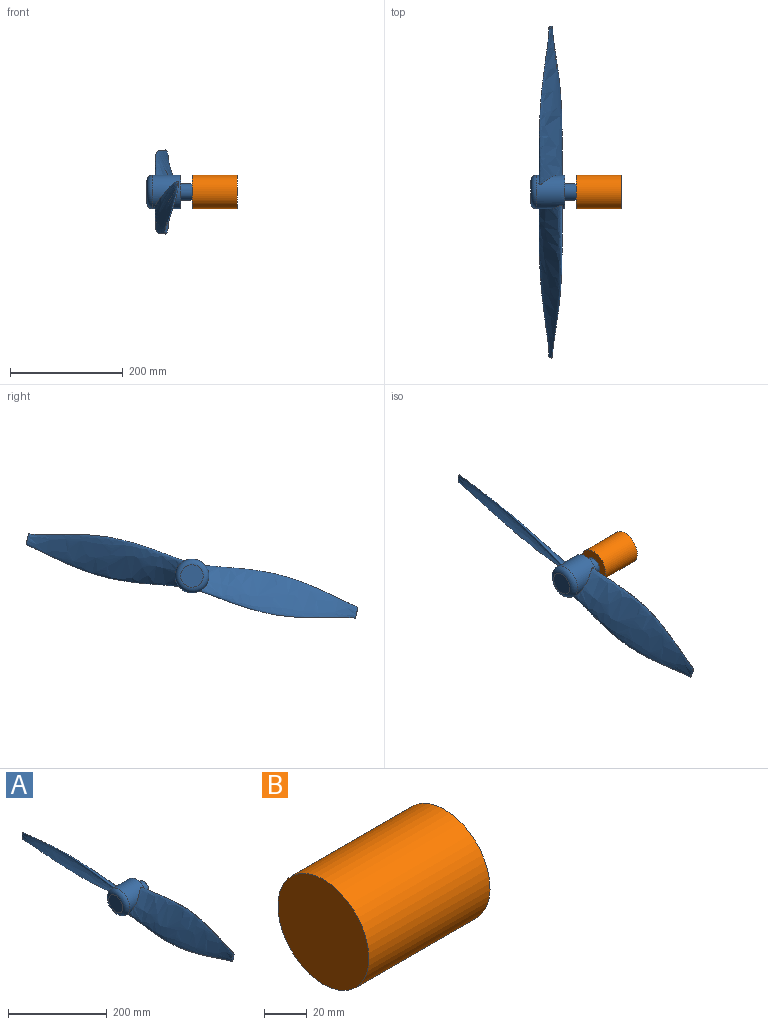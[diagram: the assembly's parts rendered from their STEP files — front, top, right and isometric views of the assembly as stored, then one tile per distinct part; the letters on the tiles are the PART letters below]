
ASSEMBLY  parts=2 mates=1
PART A: 15 faces, bbox 80x600x95 mm
  f0: plane 30x30mm, normal (1,0,0), area 624.5mm2, adj f1,f6,f7,f8,f9
  f1: cylinder r=15mm len=30mm, axis (-1,0,0), area 1885mm2, adj f0,f2
  f2: plane 60x60mm, normal (1,0,0), area 2120.6mm2, adj f1,f3
  f3: cylinder r=30mm len=60mm, axis (-1,0,0), area 8074.1mm2, adj f2,f5,f12,f13
  f4: plane 40x40mm, normal (-1,0,0), area 1256.6mm2, adj f5
  f5: torus R=20mm, axis (1,0,0), area 2602.2mm2, adj f3,f4
  f6: plane 20x2mm, normal (0,-1,0), area 40mm2, adj f0,f7,f9,f10
  f7: cylinder r=5mm len=20mm, axis (1,0,0), area 588mm2, adj f0,f6,f8,f10
  f8: plane 20x2mm, normal (0,1,0), area 40mm2, adj f0,f7,f9,f10
  f9: plane 20x2mm, normal (0,0,1), area 40mm2, adj f0,f6,f8,f10
  f10: plane 11.9x10mm, normal (1,0,0), area 82.4mm2, adj f6,f7,f8,f9
  f11: plane 19.74x6.03mm, normal (0,1,0), area 78.5mm2, adj f12
  f12: bspline ~300x95.03mm, area 35769mm2, adj f3,f11
  f13: bspline ~300x95.03mm, area 35769mm2, adj f3,f14
  f14: plane 19.74x6.03mm, normal (0,-1,0), area 78.5mm2, adj f13
PART B: 5 faces, bbox 95x60x60 mm
  f0: plane 60x60mm, normal (-1,0,0), area 2827.4mm2, adj f4
  f1: plane 10x10mm, normal (1,0,0), area 78.5mm2, adj f2
  f2: cylinder r=5mm len=15mm, axis (-1,0,0), area 471.2mm2, adj f1,f3
  f3: plane 60x60mm, normal (1,0,0), area 2748.9mm2, adj f2,f4
  f4: cylinder r=30mm len=80mm, axis (-1,0,0), area 15079.6mm2, adj f0,f3
PLACE A rot(axis=(-1,0,0),167.5deg) t=(-13.39,18.9,112.47)mm
PLACE B rot(axis=(0,1,0),180deg) t=(111.61,18.9,112.47)mm fixed
MATE revolute A.f7 <-> B.f2  axis (1,0,0) through (31.61,18.9,112.47)mm
